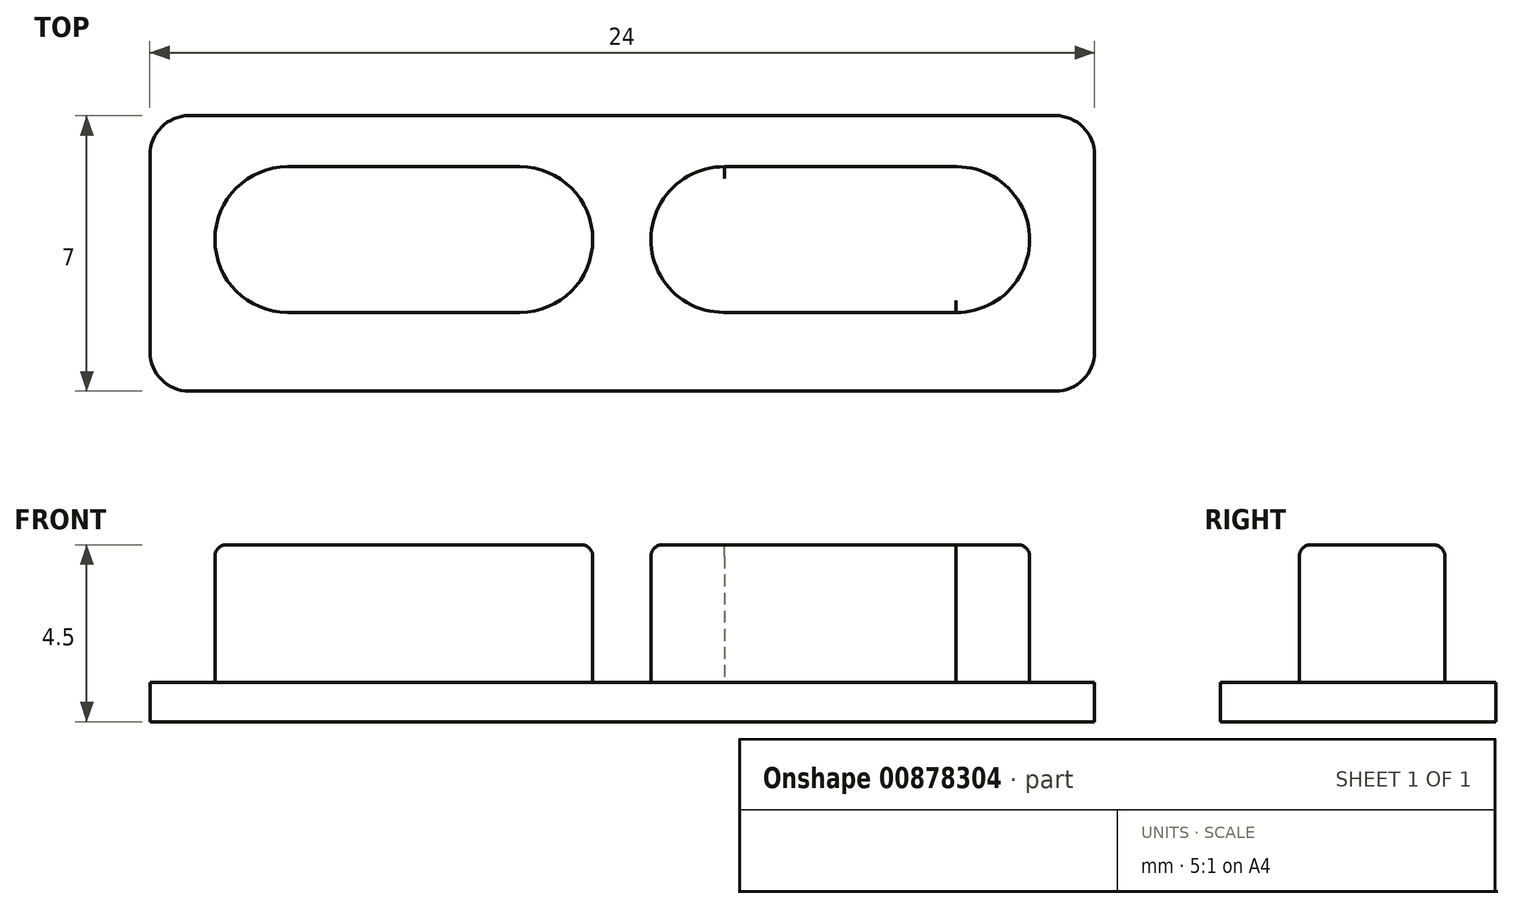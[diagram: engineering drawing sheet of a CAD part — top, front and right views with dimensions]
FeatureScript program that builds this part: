
annotation { "Feature Type Name" : "Feature", "Feature Type Description" : "" }
export const myFeature = defineFeature(function(context is Context, id is Id, definition is map)
    precondition{}
    {
        {
            var Q0;
            Q0=qCreatedBy(makeId("Top.planeOp"),FACE);
            var sketch = newSketch(context, id + "F0", { "sketchPlane" : qUnion([Q0])});
            skLineSegment(sketch, "E0.bottom", {"start": v(-13.04, 4.05) * mm, "end": v(10.96, 4.05) * mm});
            skLineSegment(sketch, "E0.top", {"start": v(-13.04, -2.95) * mm, "end": v(10.96, -2.95) * mm});
            skLineSegment(sketch, "E0.left", {"start": v(-13.04, 4.05) * mm, "end": v(-13.04, -2.95) * mm});
            skLineSegment(sketch, "E0.right", {"start": v(10.96, 4.05) * mm, "end": v(10.96, -2.95) * mm});
            skSolve(sketch);
        }
        {
            var Q0;
            Q0 = qSketchRegion(id + "F0", true);
            extrude(context, id + "F1", {"entities" : qUnion([Q0]), "depth" : 1 * mm, "offsetDistance" : 25 * mm});
        }
        {
            var Q0;
            Q0=makeQuery(id+"F1.opExtrude","CAP_FACE",FACE,{"disambiguationData":[OSD([sQuery(id+"F0.wireOp",EDGE,"E0.bottom"),sQuery(id+"F0.wireOp",EDGE,"E0.top"),sQuery(id+"F0.wireOp",EDGE,"E0.left"),sQuery(id+"F0.wireOp",EDGE,"E0.right")])],"isStart":false});
            var sketch = newSketch(context, id + "F2", { "sketchPlane" : qUnion([Q0])});
            skLineSegment(sketch, "E1", {"start": v(-9.54, 2.75) * mm, "end": v(-3.64, 2.75) * mm});
            skLineSegment(sketch, "E2", {"start": v(-9.54, -0.95) * mm, "end": v(-3.64, -0.95) * mm});
            skArc(sketch, "E3", {"start": v(-9.54, 2.75) * mm, "mid": v(-11.39, 0.9) * mm, "end": v(-9.54, -0.95) * mm});
            skArc(sketch, "E4", {"start": v(-3.64, -0.95) * mm, "mid": v(-1.79, 0.9) * mm, "end": v(-3.64, 2.75) * mm});
            skLineSegment(sketch, "E5", {"start": v(1.56, 2.75) * mm, "end": v(7.46, 2.75) * mm});
            skLineSegment(sketch, "E6", {"start": v(1.54, -0.95) * mm, "end": v(7.44, -0.95) * mm});
            skArc(sketch, "E7", {"start": v(1.56, 2.75) * mm, "mid": v(-0.3, 0.91) * mm, "end": v(1.54, -0.95) * mm});
            skArc(sketch, "E8", {"start": v(7.44, -0.95) * mm, "mid": v(9.31, 0.9) * mm, "end": v(7.46, 2.75) * mm});
            skSolve(sketch);
        }
        {
            var Q0;
            Q0=makeQuery(id+"F2.imprint","IMPRINT",FACE,{"disambiguationData":[TD([[makeQuery(id+"F2.imprint","IMPRINT",EDGE,{"derivedFrom":sQuery(id+"F2.wireOp",EDGE,"E1")}),-1.0]])]});
            var Q1;
            Q1=makeQuery(id+"F2.imprint","IMPRINT",FACE,{"disambiguationData":[TD([[makeQuery(id+"F2.imprint","IMPRINT",EDGE,{"derivedFrom":sQuery(id+"F2.wireOp",EDGE,"E5")}),-1.0]])]});
            extrude(context, id + "F3", {"entities" : qUnion([Q0, Q1]), "operationType" : NewBodyOperationType.ADD, "depth" : 3.5 * mm, "offsetDistance" : 25 * mm});
        }
        {
            var Q0;
            Q0=makeQuery(id+"F1.opExtrude","SWEPT_EDGE",EDGE,{"disambiguationData":[OSD([sQuery(id+"F0.wireOp",EDGE,"E0.top"),sQuery(id+"F0.wireOp",EDGE,"E0.left")])]});
            var Q1;
            Q1=makeQuery(id+"F1.opExtrude","SWEPT_EDGE",EDGE,{"disambiguationData":[OSD([sQuery(id+"F0.wireOp",EDGE,"E0.top"),sQuery(id+"F0.wireOp",EDGE,"E0.right")])]});
            var Q2;
            Q2=makeQuery(id+"F1.opExtrude","SWEPT_EDGE",EDGE,{"disambiguationData":[OSD([sQuery(id+"F0.wireOp",EDGE,"E0.bottom"),sQuery(id+"F0.wireOp",EDGE,"E0.right")])]});
            var Q3;
            Q3=makeQuery(id+"F1.opExtrude","SWEPT_EDGE",EDGE,{"disambiguationData":[OSD([sQuery(id+"F0.wireOp",EDGE,"E0.bottom"),sQuery(id+"F0.wireOp",EDGE,"E0.left")])]});
            fillet(context, id + "F4", {"entities" : qUnion([Q0, Q1, Q2, Q3]), "radius" : 1 * mm, "tangentPropagation" : true, "allowEdgeOverflow" : false});
        }
        {
            var Q0;
            Q0=makeQuery(id+"F3.opExtrude","CAP_EDGE",EDGE,{"disambiguationData":[OSD([sQuery(id+"F2.wireOp",EDGE,"E1")])],"isStart":false});
            var Q1;
            Q1=makeQuery(id+"F3.opExtrude","CAP_EDGE",EDGE,{"disambiguationData":[OSD([sQuery(id+"F2.wireOp",EDGE,"E5")])],"isStart":false});
            var Q2;
            Q2=makeQuery(id+"F3.opExtrude","CAP_EDGE",EDGE,{"disambiguationData":[OSD([sQuery(id+"F2.wireOp",EDGE,"E7")])],"isStart":false});
            fillet(context, id + "F5", {"entities" : qUnion([Q0, Q1, Q2]), "radius" : 0.3 * mm, "tangentPropagation" : true, "allowEdgeOverflow" : false});
        }
    });
